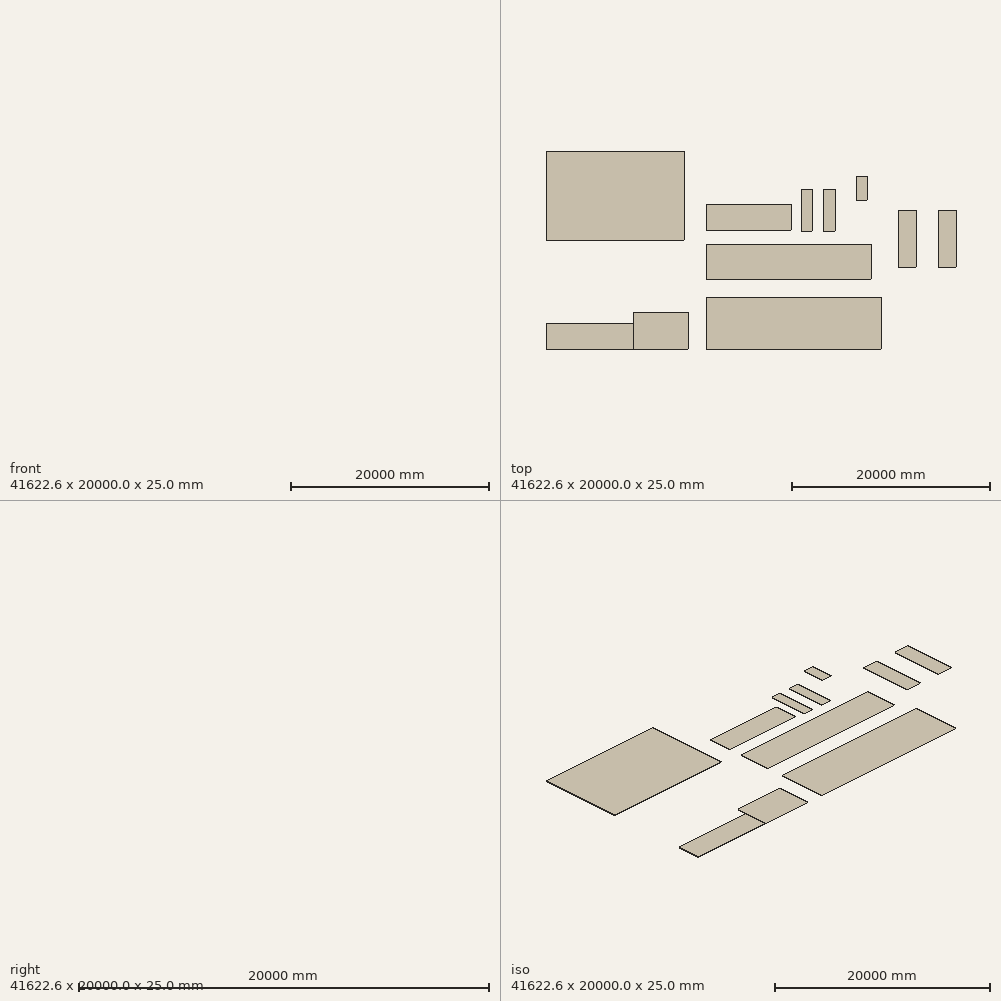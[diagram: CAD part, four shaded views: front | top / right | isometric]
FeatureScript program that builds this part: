
annotation { "Feature Type Name" : "Feature", "Feature Type Description" : "" }
export const myFeature = defineFeature(function(context is Context, id is Id, definition is map)
    precondition{}
    {
        {
            var Q0;
            Q0=qCreatedBy(makeId("Top.planeOp"),FACE);
            var sketch = newSketch(context, id + "F0", { "sketchPlane" : qUnion([Q0])});
            skLineSegment(sketch, "E0.bottom", {"start": v(21000, -10000) * mm, "end": v(-21000, -10000) * mm});
            skLineSegment(sketch, "E0.top", {"start": v(21000, 10000) * mm, "end": v(-21000, 10000) * mm});
            skLineSegment(sketch, "E0.left", {"start": v(21000, -10000) * mm, "end": v(21000, 10000) * mm});
            skLineSegment(sketch, "E0.right", {"start": v(-21000, -10000) * mm, "end": v(-21000, 10000) * mm});
            skLineSegment(sketch, "E1", {"start": v(-7000, 10000) * mm, "end": v(-7000, 1000) * mm});
            skLineSegment(sketch, "E2", {"start": v(-7000, 1000) * mm, "end": v(-21000, 1000) * mm});
            skLineSegment(sketch, "E3", {"start": v(-21000, -7440.34) * mm, "end": v(-12160.65, -7440.34) * mm});
            skLineSegment(sketch, "E4", {"start": v(-12160.65, -7440.34) * mm, "end": v(-12160.65, -10000) * mm});
            skLineSegment(sketch, "E5", {"start": v(-12160.65, -7440.34) * mm, "end": v(-12160.65, -6265.54) * mm});
            skLineSegment(sketch, "E6", {"start": v(-12160.65, -6265.54) * mm, "end": v(-6566.4, -6265.54) * mm});
            skLineSegment(sketch, "E7", {"start": v(-6566.4, -6265.54) * mm, "end": v(-6566.4, -10000) * mm});
            skLineSegment(sketch, "E8", {"start": v(-4776.23, -10000) * mm, "end": v(-4776.23, -4763.34) * mm});
            skLineSegment(sketch, "E9", {"start": v(-4776.23, -4763.34) * mm, "end": v(12957.58, -4763.34) * mm});
            skLineSegment(sketch, "E10", {"start": v(12957.58, -4763.34) * mm, "end": v(12957.58, -10000) * mm});
            skLineSegment(sketch, "E11.bottom", {"start": v(13517, -10000) * mm, "end": v(15530.94, -10000) * mm});
            skLineSegment(sketch, "E11.top", {"start": v(13517, -4763.34) * mm, "end": v(15530.94, -4763.34) * mm});
            skLineSegment(sketch, "E11.left", {"start": v(13517, -10000) * mm, "end": v(13517, -4763.34) * mm});
            skLineSegment(sketch, "E11.right", {"start": v(15530.94, -10000) * mm, "end": v(15530.94, -4763.34) * mm});
            skLineSegment(sketch, "E12.bottom", {"start": v(21000, -10000) * mm, "end": v(15978.48, -10000) * mm});
            skLineSegment(sketch, "E12.top", {"start": v(21000, -4763.34) * mm, "end": v(15978.48, -4763.34) * mm});
            skLineSegment(sketch, "E12.left", {"start": v(21000, -10000) * mm, "end": v(21000, -4763.34) * mm});
            skLineSegment(sketch, "E12.right", {"start": v(15978.48, -10000) * mm, "end": v(15978.48, -4763.34) * mm});
            skLineSegment(sketch, "E13.bottom", {"start": v(18831.56, 4083.84) * mm, "end": v(20622.63, 4083.84) * mm});
            skLineSegment(sketch, "E13.top", {"start": v(18831.56, -1734.2) * mm, "end": v(20622.63, -1734.2) * mm});
            skLineSegment(sketch, "E13.left", {"start": v(18831.56, 4083.84) * mm, "end": v(18831.56, -1734.2) * mm});
            skLineSegment(sketch, "E13.right", {"start": v(20622.63, 4083.84) * mm, "end": v(20622.63, -1734.2) * mm});
            skLineSegment(sketch, "E14.bottom", {"start": v(14747.75, 4083.84) * mm, "end": v(16538.82, 4083.84) * mm});
            skLineSegment(sketch, "E14.top", {"start": v(14747.75, -1734.2) * mm, "end": v(16538.82, -1734.2) * mm});
            skLineSegment(sketch, "E14.left", {"start": v(14747.75, 4083.84) * mm, "end": v(14747.75, -1734.2) * mm});
            skLineSegment(sketch, "E14.right", {"start": v(16538.82, 4083.84) * mm, "end": v(16538.82, -1734.2) * mm});
            skLineSegment(sketch, "E15.bottom", {"start": v(15475, 10000) * mm, "end": v(21000, 10000) * mm});
            skLineSegment(sketch, "E15.top", {"start": v(15475, 5538.35) * mm, "end": v(21000, 5538.35) * mm});
            skLineSegment(sketch, "E15.left", {"start": v(15475, 10000) * mm, "end": v(15475, 5538.35) * mm});
            skLineSegment(sketch, "E15.right", {"start": v(21000, 10000) * mm, "end": v(21000, 5538.35) * mm});
            skLineSegment(sketch, "E16.bottom", {"start": v(-636.47, 10000) * mm, "end": v(2720.08, 10000) * mm});
            skLineSegment(sketch, "E16.top", {"start": v(-636.47, 7104.74) * mm, "end": v(2720.08, 7104.74) * mm});
            skLineSegment(sketch, "E16.left", {"start": v(-636.47, 10000) * mm, "end": v(-636.47, 7104.74) * mm});
            skLineSegment(sketch, "E16.right", {"start": v(2720.08, 10000) * mm, "end": v(2720.08, 7104.74) * mm});
            skLineSegment(sketch, "E17.bottom", {"start": v(11614.96, 10000) * mm, "end": v(14076.44, 10000) * mm});
            skLineSegment(sketch, "E17.top", {"start": v(11614.96, 8298.65) * mm, "end": v(14076.44, 8298.65) * mm});
            skLineSegment(sketch, "E17.left", {"start": v(11614.96, 10000) * mm, "end": v(11614.96, 8298.65) * mm});
            skLineSegment(sketch, "E17.right", {"start": v(14076.44, 10000) * mm, "end": v(14076.44, 8298.65) * mm});
            skLineSegment(sketch, "E18.bottom", {"start": v(10440.17, 7552.28) * mm, "end": v(11614.96, 7552.28) * mm});
            skLineSegment(sketch, "E18.top", {"start": v(10440.17, 5090.8) * mm, "end": v(11614.96, 5090.8) * mm});
            skLineSegment(sketch, "E18.left", {"start": v(10440.17, 7552.28) * mm, "end": v(10440.17, 5090.8) * mm});
            skLineSegment(sketch, "E18.right", {"start": v(11614.96, 7552.28) * mm, "end": v(11614.96, 5090.8) * mm});
            skLineSegment(sketch, "E19.bottom", {"start": v(8311, 6209.66) * mm, "end": v(7137.88, 6209.66) * mm});
            skLineSegment(sketch, "E19.top", {"start": v(8311, 1902.08) * mm, "end": v(7137.88, 1902.08) * mm});
            skLineSegment(sketch, "E19.left", {"start": v(8311, 6209.66) * mm, "end": v(8311, 1902.08) * mm});
            skLineSegment(sketch, "E19.right", {"start": v(7137.88, 6209.66) * mm, "end": v(7137.88, 1902.08) * mm});
            skLineSegment(sketch, "E20.bottom", {"start": v(5962.89, 6209.66) * mm, "end": v(4845.9, 6209.66) * mm});
            skLineSegment(sketch, "E20.top", {"start": v(5962.89, 1902.08) * mm, "end": v(4845.9, 1902.08) * mm});
            skLineSegment(sketch, "E20.left", {"start": v(5962.89, 6209.66) * mm, "end": v(5962.89, 1902.08) * mm});
            skLineSegment(sketch, "E20.right", {"start": v(4845.9, 6209.66) * mm, "end": v(4845.9, 1902.08) * mm});
            skLineSegment(sketch, "E21.bottom", {"start": v(-4776.23, 4633.95) * mm, "end": v(3894.88, 4633.95) * mm});
            skLineSegment(sketch, "E21.top", {"start": v(-4776.23, 2079.56) * mm, "end": v(3894.88, 2079.56) * mm});
            skLineSegment(sketch, "E21.left", {"start": v(-4776.23, 4633.95) * mm, "end": v(-4776.23, 2079.56) * mm});
            skLineSegment(sketch, "E21.right", {"start": v(3894.88, 4633.95) * mm, "end": v(3894.88, 2079.56) * mm});
            skLineSegment(sketch, "E22.bottom", {"start": v(-7517.42, 1000) * mm, "end": v(-10762.09, 1000) * mm});
            skLineSegment(sketch, "E22.top", {"start": v(-7517.42, -1062.88) * mm, "end": v(-10762.09, -1062.88) * mm});
            skLineSegment(sketch, "E22.left", {"start": v(-7517.42, 1000) * mm, "end": v(-7517.42, -1062.88) * mm});
            skLineSegment(sketch, "E22.right", {"start": v(-10762.09, 1000) * mm, "end": v(-10762.09, -1062.88) * mm});
            skLineSegment(sketch, "E23.bottom", {"start": v(-12552.25, 1000) * mm, "end": v(-15796.92, 1000) * mm});
            skLineSegment(sketch, "E23.top", {"start": v(-12552.25, -1062.88) * mm, "end": v(-15796.92, -1062.88) * mm});
            skLineSegment(sketch, "E23.left", {"start": v(-12552.25, 1000) * mm, "end": v(-12552.25, -1062.88) * mm});
            skLineSegment(sketch, "E23.right", {"start": v(-15796.92, 1000) * mm, "end": v(-15796.92, -1062.88) * mm});
            skLineSegment(sketch, "E24.bottom", {"start": v(-4776.23, -2908.99) * mm, "end": v(11950.62, -2908.99) * mm});
            skLineSegment(sketch, "E24.top", {"start": v(-4776.23, 615.4) * mm, "end": v(11950.62, 615.4) * mm});
            skLineSegment(sketch, "E24.left", {"start": v(-4776.23, -2908.99) * mm, "end": v(-4776.23, 615.4) * mm});
            skLineSegment(sketch, "E24.right", {"start": v(11950.62, -2908.99) * mm, "end": v(11950.62, 615.4) * mm});
            skLineSegment(sketch, "E25", {"start": v(-636.47, 7552.28) * mm, "end": v(-7000, 7552.28) * mm, "construction": true});
            skLineSegment(sketch, "E26", {"start": v(2720.08, 7552.28) * mm, "end": v(8393.2, 7552.28) * mm, "construction": true});
            skLineSegment(sketch, "E27", {"start": v(8393.2, 7552.28) * mm, "end": v(8393.2, 10000) * mm, "construction": true});
            skLineSegment(sketch, "E28", {"start": v(-5839.14, -4763.34) * mm, "end": v(-5839.14, -10000) * mm, "construction": true});
            skLineSegment(sketch, "E29", {"start": v(-5839.14, -4763.34) * mm, "end": v(-4776.23, -4763.34) * mm, "construction": true});
            skLineSegment(sketch, "E30", {"start": v(1041.8, -2908.99) * mm, "end": v(1041.8, -3804.07) * mm, "construction": true});
            skLineSegment(sketch, "E31", {"start": v(1041.8, -3804.07) * mm, "end": v(3615.17, -3804.07) * mm, "construction": true});
            skLineSegment(sketch, "E32", {"start": v(3615.17, -3804.07) * mm, "end": v(3615.17, -2908.99) * mm, "construction": true});
            skSolve(sketch);
        }
        {
            var Q0;
            {var subQ1=sQuery(id+"F0.wireOp",EDGE,"E1");Q0=makeQuery(id+"F0.imprint","IMPRINT",FACE,{"disambiguationData":[TD([[makeQuery(id+"F0.imprint","IMPRINT",EDGE,{"derivedFrom":subQ1}),-1.0]])]});}
            var Q1;
            {var subQ4=sQuery(id+"F0.wireOp",EDGE,"E3");Q1=makeQuery(id+"F0.imprint","IMPRINT",FACE,{"disambiguationData":[TD([[makeQuery(id+"F0.imprint","IMPRINT",EDGE,{"derivedFrom":subQ4}),-1.0]])]});}
            extrude(context, id + "F1", {"entities" : qUnion([Q0, Q1]), "depth" : 25 * mm});
        }
        {
            var Q0;
            {var subQ0=sQuery(id+"F0.wireOp",EDGE,"E4");Q0=makeQuery(id+"F0.imprint","IMPRINT",FACE,{"disambiguationData":[TD([[makeQuery(id+"F0.imprint","IMPRINT",EDGE,{"derivedFrom":subQ0}),1.0]])]});}
            var Q1;
            {var subQ0=sQuery(id+"F0.wireOp",EDGE,"E8");Q1=makeQuery(id+"F0.imprint","IMPRINT",FACE,{"disambiguationData":[TD([[makeQuery(id+"F0.imprint","IMPRINT",EDGE,{"derivedFrom":subQ0}),-1.0]])]});}
            var Q2;
            Q2=makeQuery(id+"F0.imprint","IMPRINT",FACE,{"disambiguationData":[TD([[makeQuery(id+"F0.imprint","IMPRINT",EDGE,{"derivedFrom":sQuery(id+"F0.wireOp",EDGE,"E24.bottom")}),1.0]])]});
            var Q3;
            Q3=makeQuery(id+"F0.imprint","IMPRINT",FACE,{"disambiguationData":[TD([[makeQuery(id+"F0.imprint","IMPRINT",EDGE,{"derivedFrom":sQuery(id+"F0.wireOp",EDGE,"E21.bottom")}),-1.0]])]});
            var Q4;
            Q4=makeQuery(id+"F0.imprint","IMPRINT",FACE,{"disambiguationData":[TD([[makeQuery(id+"F0.imprint","IMPRINT",EDGE,{"derivedFrom":sQuery(id+"F0.wireOp",EDGE,"E11.bottom")}),1.0]])]});
            var Q5;
            Q5=makeQuery(id+"F0.imprint","IMPRINT",FACE,{"disambiguationData":[TD([[makeQuery(id+"F0.imprint","IMPRINT",EDGE,{"derivedFrom":sQuery(id+"F0.wireOp",EDGE,"E12.bottom")}),-1.0]])]});
            var Q6;
            Q6=makeQuery(id+"F0.imprint","IMPRINT",FACE,{"disambiguationData":[TD([[makeQuery(id+"F0.imprint","IMPRINT",EDGE,{"derivedFrom":sQuery(id+"F0.wireOp",EDGE,"E14.bottom")}),-1.0]])]});
            var Q7;
            Q7=makeQuery(id+"F0.imprint","IMPRINT",FACE,{"disambiguationData":[TD([[makeQuery(id+"F0.imprint","IMPRINT",EDGE,{"derivedFrom":sQuery(id+"F0.wireOp",EDGE,"E13.bottom")}),-1.0]])]});
            var Q8;
            Q8=makeQuery(id+"F0.imprint","IMPRINT",FACE,{"disambiguationData":[TD([[makeQuery(id+"F0.imprint","IMPRINT",EDGE,{"derivedFrom":sQuery(id+"F0.wireOp",EDGE,"E20.bottom")}),1.0]])]});
            var Q9;
            Q9=makeQuery(id+"F0.imprint","IMPRINT",FACE,{"disambiguationData":[TD([[makeQuery(id+"F0.imprint","IMPRINT",EDGE,{"derivedFrom":sQuery(id+"F0.wireOp",EDGE,"E19.bottom")}),1.0]])]});
            var Q10;
            Q10=makeQuery(id+"F0.imprint","IMPRINT",FACE,{"disambiguationData":[TD([[makeQuery(id+"F0.imprint","IMPRINT",EDGE,{"derivedFrom":sQuery(id+"F0.wireOp",EDGE,"E18.bottom")}),-1.0]])]});
            var Q11;
            Q11=makeQuery(id+"F0.imprint","IMPRINT",FACE,{"disambiguationData":[TD([[makeQuery(id+"F0.imprint","IMPRINT",EDGE,{"derivedFrom":sQuery(id+"F0.wireOp",EDGE,"E17.bottom")}),-1.0]])]});
            var Q12;
            Q12=makeQuery(id+"F0.imprint","IMPRINT",FACE,{"disambiguationData":[TD([[makeQuery(id+"F0.imprint","IMPRINT",EDGE,{"derivedFrom":sQuery(id+"F0.wireOp",EDGE,"E15.bottom")}),-1.0]])]});
            var Q13;
            Q13=makeQuery(id+"F0.imprint","IMPRINT",FACE,{"disambiguationData":[TD([[makeQuery(id+"F0.imprint","IMPRINT",EDGE,{"derivedFrom":sQuery(id+"F0.wireOp",EDGE,"E16.bottom")}),-1.0]])]});
            var Q14;
            Q14=makeQuery(id+"F0.imprint","IMPRINT",FACE,{"disambiguationData":[TD([[makeQuery(id+"F0.imprint","IMPRINT",EDGE,{"derivedFrom":sQuery(id+"F0.wireOp",EDGE,"E22.bottom")}),1.0]])]});
            var Q15;
            Q15=makeQuery(id+"F0.imprint","IMPRINT",FACE,{"disambiguationData":[TD([[makeQuery(id+"F0.imprint","IMPRINT",EDGE,{"derivedFrom":sQuery(id+"F0.wireOp",EDGE,"E23.bottom")}),1.0]])]});
            extrude(context, id + "F2", {"entities" : qUnion([Q0, Q1, Q2, Q3, Q4, Q5, Q6, Q7, Q8, Q9, Q10, Q11, Q12, Q13, Q14, Q15]), "depth" : 5 * mm});
        }
    });
